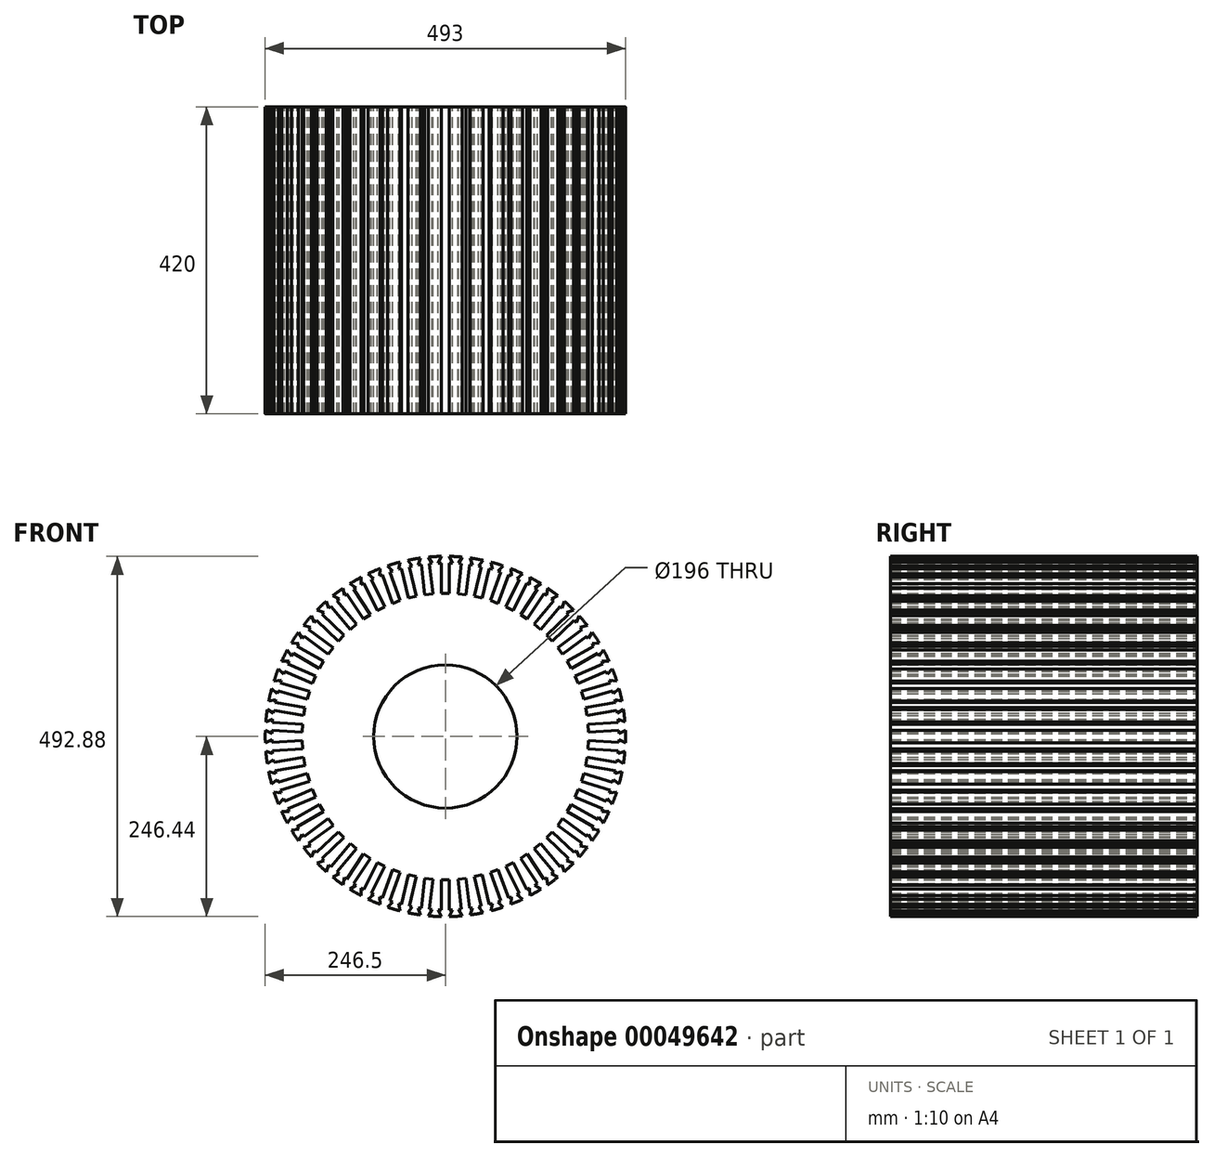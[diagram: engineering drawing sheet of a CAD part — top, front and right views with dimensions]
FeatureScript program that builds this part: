
annotation { "Feature Type Name" : "Feature", "Feature Type Description" : "" }
export const myFeature = defineFeature(function(context is Context, id is Id, definition is map)
    precondition{}
    {
        {
            var Q0;
            Q0=qCreatedBy(makeId("Front.planeOp"),FACE);
            var sketch = newSketch(context, id + "F0", { "sketchPlane" : qUnion([Q0])});
            skArc(sketch, "E0", {"start": v(-5.6, 246.44) * mm, "mid": v(-14.33, 246.08) * mm, "end": v(-23.05, 245.42) * mm});
            skLineSegment(sketch, "E1", {"start": v(0, -271.23) * mm, "end": v(0, 264.46) * mm, "construction": true});
            skLineSegment(sketch, "E2", {"start": v(0, 195.84) * mm, "end": v(-5.6, 195.84) * mm});
            skLineSegment(sketch, "E3", {"start": v(-5.6, 195.84) * mm, "end": v(-5.6, 237.27) * mm});
            skLineSegment(sketch, "E4.MirrorCS", {"start": v(5.6, 195.84) * mm, "end": v(5.6, 237.27) * mm});
            skLineSegment(sketch, "E5.MirrorCS", {"start": v(0, 195.84) * mm, "end": v(5.6, 195.84) * mm});
            skLineSegment(sketch, "E6", {"start": v(-5.6, 237.27) * mm, "end": v(-9.6, 237.27) * mm});
            skLineSegment(sketch, "E7", {"start": v(-9.6, 237.27) * mm, "end": v(-5.6, 246.44) * mm});
            skLineSegment(sketch, "E8.MirrorCS", {"start": v(9.6, 237.27) * mm, "end": v(5.6, 246.44) * mm});
            skLineSegment(sketch, "E9.MirrorCS", {"start": v(5.6, 237.27) * mm, "end": v(9.6, 237.27) * mm});
            skPoint(sketch, "E10.orphan", {"position": v(5.6, 246.44) * mm});
            skLineSegment(sketch, "E11.1.0", {"start": v(28.3, 193.86) * mm, "end": v(33.1, 235.02) * mm});
            skLineSegment(sketch, "E11.1.1", {"start": v(33.1, 235.02) * mm, "end": v(37.08, 234.55) * mm});
            skLineSegment(sketch, "E11.1.2", {"start": v(37.08, 234.55) * mm, "end": v(34.17, 244.12) * mm});
            skLineSegment(sketch, "E11.1.3", {"start": v(22.74, 194.51) * mm, "end": v(28.3, 193.86) * mm});
            skLineSegment(sketch, "E11.1.4", {"start": v(22.74, 194.51) * mm, "end": v(17.17, 195.16) * mm});
            skLineSegment(sketch, "E11.1.5", {"start": v(17.17, 195.16) * mm, "end": v(21.98, 236.32) * mm});
            skLineSegment(sketch, "E11.1.6", {"start": v(21.98, 236.32) * mm, "end": v(18.01, 236.78) * mm});
            skLineSegment(sketch, "E11.1.7", {"start": v(18.01, 236.78) * mm, "end": v(23.05, 245.42) * mm});
            skLineSegment(sketch, "E11.2.0", {"start": v(50.61, 189.27) * mm, "end": v(60.17, 229.58) * mm});
            skLineSegment(sketch, "E11.2.1", {"start": v(60.17, 229.58) * mm, "end": v(64.06, 228.66) * mm});
            skLineSegment(sketch, "E11.2.2", {"start": v(64.06, 228.66) * mm, "end": v(62.28, 238.5) * mm});
            skLineSegment(sketch, "E11.2.3", {"start": v(45.16, 190.56) * mm, "end": v(50.61, 189.27) * mm});
            skLineSegment(sketch, "E11.2.4", {"start": v(45.16, 190.56) * mm, "end": v(39.71, 191.85) * mm});
            skLineSegment(sketch, "E11.2.5", {"start": v(39.71, 191.85) * mm, "end": v(49.27, 232.17) * mm});
            skLineSegment(sketch, "E11.2.6", {"start": v(49.27, 232.17) * mm, "end": v(45.38, 233.09) * mm});
            skLineSegment(sketch, "E11.2.7", {"start": v(45.38, 233.09) * mm, "end": v(51.38, 241.09) * mm});
            skLineSegment(sketch, "E11.3.0", {"start": v(72.24, 182.11) * mm, "end": v(86.41, 221.05) * mm});
            skLineSegment(sketch, "E11.3.1", {"start": v(86.41, 221.05) * mm, "end": v(90.17, 219.68) * mm});
            skLineSegment(sketch, "E11.3.2", {"start": v(90.17, 219.68) * mm, "end": v(89.55, 229.66) * mm});
            skLineSegment(sketch, "E11.3.3", {"start": v(66.98, 184.03) * mm, "end": v(72.24, 182.11) * mm});
            skLineSegment(sketch, "E11.3.4", {"start": v(66.98, 184.03) * mm, "end": v(61.72, 185.94) * mm});
            skLineSegment(sketch, "E11.3.5", {"start": v(61.72, 185.94) * mm, "end": v(75.89, 224.88) * mm});
            skLineSegment(sketch, "E11.3.6", {"start": v(75.89, 224.88) * mm, "end": v(72.13, 226.25) * mm});
            skLineSegment(sketch, "E11.3.7", {"start": v(72.13, 226.25) * mm, "end": v(79.02, 233.49) * mm});
            skLineSegment(sketch, "E11.4.0", {"start": v(92.9, 172.5) * mm, "end": v(111.5, 209.52) * mm});
            skLineSegment(sketch, "E11.4.1", {"start": v(111.5, 209.52) * mm, "end": v(115.07, 207.72) * mm});
            skLineSegment(sketch, "E11.4.2", {"start": v(115.07, 207.72) * mm, "end": v(115.6, 217.71) * mm});
            skLineSegment(sketch, "E11.4.3", {"start": v(87.9, 175) * mm, "end": v(92.9, 172.5) * mm});
            skLineSegment(sketch, "E11.4.4", {"start": v(87.9, 175) * mm, "end": v(82.89, 177.52) * mm});
            skLineSegment(sketch, "E11.4.5", {"start": v(82.89, 177.52) * mm, "end": v(101.48, 214.55) * mm});
            skLineSegment(sketch, "E11.4.6", {"start": v(101.48, 214.55) * mm, "end": v(97.9, 216.34) * mm});
            skLineSegment(sketch, "E11.4.7", {"start": v(97.9, 216.34) * mm, "end": v(105.6, 222.74) * mm});
            skLineSegment(sketch, "E11.5.0", {"start": v(112.3, 160.54) * mm, "end": v(135.06, 195.16) * mm});
            skLineSegment(sketch, "E11.5.1", {"start": v(135.06, 195.16) * mm, "end": v(138.4, 192.96) * mm});
            skLineSegment(sketch, "E11.5.2", {"start": v(138.4, 192.96) * mm, "end": v(140.1, 202.82) * mm});
            skLineSegment(sketch, "E11.5.3", {"start": v(107.61, 163.62) * mm, "end": v(112.3, 160.54) * mm});
            skLineSegment(sketch, "E11.5.4", {"start": v(107.61, 163.62) * mm, "end": v(102.94, 166.7) * mm});
            skLineSegment(sketch, "E11.5.5", {"start": v(102.94, 166.7) * mm, "end": v(125.7, 201.31) * mm});
            skLineSegment(sketch, "E11.5.6", {"start": v(125.7, 201.31) * mm, "end": v(122.36, 203.51) * mm});
            skLineSegment(sketch, "E11.5.7", {"start": v(122.36, 203.51) * mm, "end": v(130.74, 208.97) * mm});
            skLineSegment(sketch, "E11.6.0", {"start": v(130.17, 146.42) * mm, "end": v(156.8, 178.16) * mm});
            skLineSegment(sketch, "E11.6.1", {"start": v(156.8, 178.16) * mm, "end": v(159.87, 175.59) * mm});
            skLineSegment(sketch, "E11.6.2", {"start": v(159.87, 175.59) * mm, "end": v(162.7, 185.18) * mm});
            skLineSegment(sketch, "E11.6.3", {"start": v(125.88, 150.02) * mm, "end": v(130.17, 146.42) * mm});
            skLineSegment(sketch, "E11.6.4", {"start": v(125.88, 150.02) * mm, "end": v(121.6, 153.62) * mm});
            skLineSegment(sketch, "E11.6.5", {"start": v(121.6, 153.62) * mm, "end": v(148.23, 185.36) * mm});
            skLineSegment(sketch, "E11.6.6", {"start": v(148.23, 185.36) * mm, "end": v(145.16, 187.93) * mm});
            skLineSegment(sketch, "E11.6.7", {"start": v(145.16, 187.93) * mm, "end": v(154.12, 192.38) * mm});
            skLineSegment(sketch, "E11.7.0", {"start": v(146.29, 130.32) * mm, "end": v(176.43, 158.75) * mm});
            skLineSegment(sketch, "E11.7.1", {"start": v(176.43, 158.75) * mm, "end": v(179.17, 155.84) * mm});
            skLineSegment(sketch, "E11.7.2", {"start": v(179.17, 155.84) * mm, "end": v(183.1, 165.04) * mm});
            skLineSegment(sketch, "E11.7.3", {"start": v(142.45, 134.4) * mm, "end": v(146.29, 130.32) * mm});
            skLineSegment(sketch, "E11.7.4", {"start": v(142.45, 134.4) * mm, "end": v(138.6, 138.46) * mm});
            skLineSegment(sketch, "E11.7.5", {"start": v(138.6, 138.46) * mm, "end": v(168.74, 166.9) * mm});
            skLineSegment(sketch, "E11.7.6", {"start": v(168.74, 166.9) * mm, "end": v(166, 169.8) * mm});
            skLineSegment(sketch, "E11.7.7", {"start": v(166, 169.8) * mm, "end": v(175.4, 173.19) * mm});
            skLineSegment(sketch, "E11.8.0", {"start": v(160.43, 112.45) * mm, "end": v(193.66, 137.2) * mm});
            skLineSegment(sketch, "E11.8.1", {"start": v(193.66, 137.2) * mm, "end": v(196.05, 133.99) * mm});
            skLineSegment(sketch, "E11.8.2", {"start": v(196.05, 133.99) * mm, "end": v(201.02, 142.67) * mm});
            skLineSegment(sketch, "E11.8.3", {"start": v(157.08, 116.95) * mm, "end": v(160.43, 112.45) * mm});
            skLineSegment(sketch, "E11.8.4", {"start": v(157.08, 116.95) * mm, "end": v(153.74, 121.44) * mm});
            skLineSegment(sketch, "E11.8.5", {"start": v(153.74, 121.44) * mm, "end": v(186.98, 146.18) * mm});
            skLineSegment(sketch, "E11.8.6", {"start": v(186.98, 146.18) * mm, "end": v(184.59, 149.39) * mm});
            skLineSegment(sketch, "E11.8.7", {"start": v(184.59, 149.39) * mm, "end": v(194.33, 151.65) * mm});
            skLineSegment(sketch, "E11.9.0", {"start": v(172.4, 93.07) * mm, "end": v(208.28, 113.79) * mm});
            skLineSegment(sketch, "E11.9.1", {"start": v(208.28, 113.79) * mm, "end": v(210.28, 110.32) * mm});
            skLineSegment(sketch, "E11.9.2", {"start": v(210.28, 110.32) * mm, "end": v(216.22, 118.37) * mm});
            skLineSegment(sketch, "E11.9.3", {"start": v(169.6, 97.92) * mm, "end": v(172.4, 93.07) * mm});
            skLineSegment(sketch, "E11.9.4", {"start": v(169.6, 97.92) * mm, "end": v(166.8, 102.77) * mm});
            skLineSegment(sketch, "E11.9.5", {"start": v(166.8, 102.77) * mm, "end": v(202.68, 123.49) * mm});
            skLineSegment(sketch, "E11.9.6", {"start": v(202.68, 123.49) * mm, "end": v(200.68, 126.95) * mm});
            skLineSegment(sketch, "E11.9.7", {"start": v(200.68, 126.95) * mm, "end": v(210.62, 128.07) * mm});
            skLineSegment(sketch, "E11.10.0", {"start": v(182.04, 72.42) * mm, "end": v(220.08, 88.84) * mm});
            skLineSegment(sketch, "E11.10.1", {"start": v(220.08, 88.84) * mm, "end": v(221.67, 85.16) * mm});
            skLineSegment(sketch, "E11.10.2", {"start": v(221.67, 85.16) * mm, "end": v(228.5, 92.47) * mm});
            skLineSegment(sketch, "E11.10.3", {"start": v(179.82, 77.57) * mm, "end": v(182.04, 72.42) * mm});
            skLineSegment(sketch, "E11.10.4", {"start": v(179.82, 77.57) * mm, "end": v(177.6, 82.7) * mm});
            skLineSegment(sketch, "E11.10.5", {"start": v(177.6, 82.7) * mm, "end": v(215.65, 99.12) * mm});
            skLineSegment(sketch, "E11.10.6", {"start": v(215.65, 99.12) * mm, "end": v(214.06, 102.8) * mm});
            skLineSegment(sketch, "E11.10.7", {"start": v(214.06, 102.8) * mm, "end": v(224.06, 102.75) * mm});
            skLineSegment(sketch, "E11.11.0", {"start": v(189.22, 50.8) * mm, "end": v(228.9, 62.69) * mm});
            skLineSegment(sketch, "E11.11.1", {"start": v(228.9, 62.69) * mm, "end": v(230.06, 58.85) * mm});
            skLineSegment(sketch, "E11.11.2", {"start": v(230.06, 58.85) * mm, "end": v(237.69, 65.31) * mm});
            skLineSegment(sketch, "E11.11.3", {"start": v(187.6, 56.17) * mm, "end": v(189.22, 50.8) * mm});
            skLineSegment(sketch, "E11.11.4", {"start": v(187.6, 56.17) * mm, "end": v(186, 61.53) * mm});
            skLineSegment(sketch, "E11.11.5", {"start": v(186, 61.53) * mm, "end": v(225.7, 73.41) * mm});
            skLineSegment(sketch, "E11.11.6", {"start": v(225.7, 73.41) * mm, "end": v(224.55, 77.25) * mm});
            skLineSegment(sketch, "E11.11.7", {"start": v(224.55, 77.25) * mm, "end": v(234.48, 76.04) * mm});
            skLineSegment(sketch, "E11.12.0", {"start": v(193.83, 28.5) * mm, "end": v(234.64, 35.69) * mm});
            skLineSegment(sketch, "E11.12.1", {"start": v(234.64, 35.69) * mm, "end": v(235.33, 31.75) * mm});
            skLineSegment(sketch, "E11.12.2", {"start": v(235.33, 31.75) * mm, "end": v(243.66, 37.28) * mm});
            skLineSegment(sketch, "E11.12.3", {"start": v(192.86, 34) * mm, "end": v(193.83, 28.5) * mm});
            skLineSegment(sketch, "E11.12.4", {"start": v(192.86, 34) * mm, "end": v(191.89, 39.52) * mm});
            skLineSegment(sketch, "E11.12.5", {"start": v(191.89, 39.52) * mm, "end": v(232.7, 46.72) * mm});
            skLineSegment(sketch, "E11.12.6", {"start": v(232.7, 46.72) * mm, "end": v(232, 50.66) * mm});
            skLineSegment(sketch, "E11.12.7", {"start": v(232, 50.66) * mm, "end": v(241.72, 48.3) * mm});
            skLineSegment(sketch, "E11.13.0", {"start": v(195.83, 5.8) * mm, "end": v(237.2, 8.2) * mm});
            skLineSegment(sketch, "E11.13.1", {"start": v(237.2, 8.2) * mm, "end": v(237.43, 4.21) * mm});
            skLineSegment(sketch, "E11.13.2", {"start": v(237.43, 4.21) * mm, "end": v(246.35, 8.74) * mm});
            skLineSegment(sketch, "E11.13.3", {"start": v(195.5, 11.39) * mm, "end": v(195.83, 5.8) * mm});
            skLineSegment(sketch, "E11.13.4", {"start": v(195.5, 11.39) * mm, "end": v(195.18, 16.98) * mm});
            skLineSegment(sketch, "E11.13.5", {"start": v(195.18, 16.98) * mm, "end": v(236.54, 19.39) * mm});
            skLineSegment(sketch, "E11.13.6", {"start": v(236.54, 19.39) * mm, "end": v(236.31, 23.38) * mm});
            skLineSegment(sketch, "E11.13.7", {"start": v(236.31, 23.38) * mm, "end": v(245.7, 19.92) * mm});
            skLineSegment(sketch, "E11.14.0", {"start": v(195.18, -16.98) * mm, "end": v(236.54, -19.39) * mm});
            skLineSegment(sketch, "E11.14.1", {"start": v(236.54, -19.39) * mm, "end": v(236.31, -23.38) * mm});
            skLineSegment(sketch, "E11.14.2", {"start": v(236.31, -23.38) * mm, "end": v(245.7, -19.92) * mm});
            skLineSegment(sketch, "E11.14.3", {"start": v(195.5, -11.39) * mm, "end": v(195.18, -16.98) * mm});
            skLineSegment(sketch, "E11.14.4", {"start": v(195.5, -11.39) * mm, "end": v(195.83, -5.8) * mm});
            skLineSegment(sketch, "E11.14.5", {"start": v(195.83, -5.8) * mm, "end": v(237.2, -8.2) * mm});
            skLineSegment(sketch, "E11.14.6", {"start": v(237.2, -8.2) * mm, "end": v(237.43, -4.21) * mm});
            skLineSegment(sketch, "E11.14.7", {"start": v(237.43, -4.21) * mm, "end": v(246.35, -8.74) * mm});
            skLineSegment(sketch, "E11.15.0", {"start": v(191.89, -39.52) * mm, "end": v(232.7, -46.72) * mm});
            skLineSegment(sketch, "E11.15.1", {"start": v(232.7, -46.72) * mm, "end": v(232, -50.66) * mm});
            skLineSegment(sketch, "E11.15.2", {"start": v(232, -50.66) * mm, "end": v(241.72, -48.3) * mm});
            skLineSegment(sketch, "E11.15.3", {"start": v(192.86, -34) * mm, "end": v(191.89, -39.52) * mm});
            skLineSegment(sketch, "E11.15.4", {"start": v(192.86, -34) * mm, "end": v(193.83, -28.5) * mm});
            skLineSegment(sketch, "E11.15.5", {"start": v(193.83, -28.5) * mm, "end": v(234.64, -35.69) * mm});
            skLineSegment(sketch, "E11.15.6", {"start": v(234.64, -35.69) * mm, "end": v(235.33, -31.75) * mm});
            skLineSegment(sketch, "E11.15.7", {"start": v(235.33, -31.75) * mm, "end": v(243.66, -37.28) * mm});
            skLineSegment(sketch, "E11.16.0", {"start": v(186, -61.53) * mm, "end": v(225.7, -73.41) * mm});
            skLineSegment(sketch, "E11.16.1", {"start": v(225.7, -73.41) * mm, "end": v(224.55, -77.25) * mm});
            skLineSegment(sketch, "E11.16.2", {"start": v(224.55, -77.25) * mm, "end": v(234.48, -76.04) * mm});
            skLineSegment(sketch, "E11.16.3", {"start": v(187.6, -56.17) * mm, "end": v(186, -61.53) * mm});
            skLineSegment(sketch, "E11.16.4", {"start": v(187.6, -56.17) * mm, "end": v(189.22, -50.8) * mm});
            skLineSegment(sketch, "E11.16.5", {"start": v(189.22, -50.8) * mm, "end": v(228.9, -62.69) * mm});
            skLineSegment(sketch, "E11.16.6", {"start": v(228.9, -62.69) * mm, "end": v(230.06, -58.85) * mm});
            skLineSegment(sketch, "E11.16.7", {"start": v(230.06, -58.85) * mm, "end": v(237.69, -65.31) * mm});
            skLineSegment(sketch, "E11.17.0", {"start": v(177.6, -82.7) * mm, "end": v(215.65, -99.12) * mm});
            skLineSegment(sketch, "E11.17.1", {"start": v(215.65, -99.12) * mm, "end": v(214.06, -102.8) * mm});
            skLineSegment(sketch, "E11.17.2", {"start": v(214.06, -102.8) * mm, "end": v(224.06, -102.75) * mm});
            skLineSegment(sketch, "E11.17.3", {"start": v(179.82, -77.57) * mm, "end": v(177.6, -82.7) * mm});
            skLineSegment(sketch, "E11.17.4", {"start": v(179.82, -77.57) * mm, "end": v(182.04, -72.42) * mm});
            skLineSegment(sketch, "E11.17.5", {"start": v(182.04, -72.42) * mm, "end": v(220.08, -88.84) * mm});
            skLineSegment(sketch, "E11.17.6", {"start": v(220.08, -88.84) * mm, "end": v(221.67, -85.16) * mm});
            skLineSegment(sketch, "E11.17.7", {"start": v(221.67, -85.16) * mm, "end": v(228.5, -92.47) * mm});
            skLineSegment(sketch, "E11.18.0", {"start": v(166.8, -102.77) * mm, "end": v(202.68, -123.49) * mm});
            skLineSegment(sketch, "E11.18.1", {"start": v(202.68, -123.49) * mm, "end": v(200.68, -126.95) * mm});
            skLineSegment(sketch, "E11.18.2", {"start": v(200.68, -126.95) * mm, "end": v(210.62, -128.07) * mm});
            skLineSegment(sketch, "E11.18.3", {"start": v(169.6, -97.92) * mm, "end": v(166.8, -102.77) * mm});
            skLineSegment(sketch, "E11.18.4", {"start": v(169.6, -97.92) * mm, "end": v(172.4, -93.07) * mm});
            skLineSegment(sketch, "E11.18.5", {"start": v(172.4, -93.07) * mm, "end": v(208.28, -113.79) * mm});
            skLineSegment(sketch, "E11.18.6", {"start": v(208.28, -113.79) * mm, "end": v(210.28, -110.32) * mm});
            skLineSegment(sketch, "E11.18.7", {"start": v(210.28, -110.32) * mm, "end": v(216.22, -118.37) * mm});
            skLineSegment(sketch, "E11.19.0", {"start": v(153.74, -121.44) * mm, "end": v(186.98, -146.18) * mm});
            skLineSegment(sketch, "E11.19.1", {"start": v(186.98, -146.18) * mm, "end": v(184.59, -149.39) * mm});
            skLineSegment(sketch, "E11.19.2", {"start": v(184.59, -149.39) * mm, "end": v(194.33, -151.65) * mm});
            skLineSegment(sketch, "E11.19.3", {"start": v(157.08, -116.95) * mm, "end": v(153.74, -121.44) * mm});
            skLineSegment(sketch, "E11.19.4", {"start": v(157.08, -116.95) * mm, "end": v(160.43, -112.45) * mm});
            skLineSegment(sketch, "E11.19.5", {"start": v(160.43, -112.45) * mm, "end": v(193.66, -137.2) * mm});
            skLineSegment(sketch, "E11.19.6", {"start": v(193.66, -137.2) * mm, "end": v(196.05, -133.99) * mm});
            skLineSegment(sketch, "E11.19.7", {"start": v(196.05, -133.99) * mm, "end": v(201.02, -142.67) * mm});
            skLineSegment(sketch, "E11.20.0", {"start": v(138.6, -138.46) * mm, "end": v(168.74, -166.9) * mm});
            skLineSegment(sketch, "E11.20.1", {"start": v(168.74, -166.9) * mm, "end": v(166, -169.8) * mm});
            skLineSegment(sketch, "E11.20.2", {"start": v(166, -169.8) * mm, "end": v(175.4, -173.19) * mm});
            skLineSegment(sketch, "E11.20.3", {"start": v(142.45, -134.4) * mm, "end": v(138.6, -138.46) * mm});
            skLineSegment(sketch, "E11.20.4", {"start": v(142.45, -134.4) * mm, "end": v(146.29, -130.32) * mm});
            skLineSegment(sketch, "E11.20.5", {"start": v(146.29, -130.32) * mm, "end": v(176.43, -158.75) * mm});
            skLineSegment(sketch, "E11.20.6", {"start": v(176.43, -158.75) * mm, "end": v(179.17, -155.84) * mm});
            skLineSegment(sketch, "E11.20.7", {"start": v(179.17, -155.84) * mm, "end": v(183.1, -165.04) * mm});
            skLineSegment(sketch, "E11.21.0", {"start": v(121.6, -153.62) * mm, "end": v(148.23, -185.36) * mm});
            skLineSegment(sketch, "E11.21.1", {"start": v(148.23, -185.36) * mm, "end": v(145.16, -187.93) * mm});
            skLineSegment(sketch, "E11.21.2", {"start": v(145.16, -187.93) * mm, "end": v(154.12, -192.38) * mm});
            skLineSegment(sketch, "E11.21.3", {"start": v(125.88, -150.02) * mm, "end": v(121.6, -153.62) * mm});
            skLineSegment(sketch, "E11.21.4", {"start": v(125.88, -150.02) * mm, "end": v(130.17, -146.42) * mm});
            skLineSegment(sketch, "E11.21.5", {"start": v(130.17, -146.42) * mm, "end": v(156.8, -178.16) * mm});
            skLineSegment(sketch, "E11.21.6", {"start": v(156.8, -178.16) * mm, "end": v(159.87, -175.59) * mm});
            skLineSegment(sketch, "E11.21.7", {"start": v(159.87, -175.59) * mm, "end": v(162.7, -185.18) * mm});
            skLineSegment(sketch, "E11.22.0", {"start": v(102.94, -166.7) * mm, "end": v(125.7, -201.31) * mm});
            skLineSegment(sketch, "E11.22.1", {"start": v(125.7, -201.31) * mm, "end": v(122.36, -203.51) * mm});
            skLineSegment(sketch, "E11.22.2", {"start": v(122.36, -203.51) * mm, "end": v(130.74, -208.97) * mm});
            skLineSegment(sketch, "E11.22.3", {"start": v(107.61, -163.62) * mm, "end": v(102.94, -166.7) * mm});
            skLineSegment(sketch, "E11.22.4", {"start": v(107.61, -163.62) * mm, "end": v(112.3, -160.54) * mm});
            skLineSegment(sketch, "E11.22.5", {"start": v(112.3, -160.54) * mm, "end": v(135.06, -195.16) * mm});
            skLineSegment(sketch, "E11.22.6", {"start": v(135.06, -195.16) * mm, "end": v(138.4, -192.96) * mm});
            skLineSegment(sketch, "E11.22.7", {"start": v(138.4, -192.96) * mm, "end": v(140.1, -202.82) * mm});
            skLineSegment(sketch, "E11.23.0", {"start": v(82.89, -177.52) * mm, "end": v(101.48, -214.55) * mm});
            skLineSegment(sketch, "E11.23.1", {"start": v(101.48, -214.55) * mm, "end": v(97.9, -216.34) * mm});
            skLineSegment(sketch, "E11.23.2", {"start": v(97.9, -216.34) * mm, "end": v(105.6, -222.74) * mm});
            skLineSegment(sketch, "E11.23.3", {"start": v(87.9, -175) * mm, "end": v(82.89, -177.52) * mm});
            skLineSegment(sketch, "E11.23.4", {"start": v(87.9, -175) * mm, "end": v(92.9, -172.5) * mm});
            skLineSegment(sketch, "E11.23.5", {"start": v(92.9, -172.5) * mm, "end": v(111.5, -209.52) * mm});
            skLineSegment(sketch, "E11.23.6", {"start": v(111.5, -209.52) * mm, "end": v(115.07, -207.72) * mm});
            skLineSegment(sketch, "E11.23.7", {"start": v(115.07, -207.72) * mm, "end": v(115.6, -217.71) * mm});
            skLineSegment(sketch, "E11.24.0", {"start": v(61.72, -185.94) * mm, "end": v(75.89, -224.88) * mm});
            skLineSegment(sketch, "E11.24.1", {"start": v(75.89, -224.88) * mm, "end": v(72.13, -226.25) * mm});
            skLineSegment(sketch, "E11.24.2", {"start": v(72.13, -226.25) * mm, "end": v(79.02, -233.49) * mm});
            skLineSegment(sketch, "E11.24.3", {"start": v(66.98, -184.03) * mm, "end": v(61.72, -185.94) * mm});
            skLineSegment(sketch, "E11.24.4", {"start": v(66.98, -184.03) * mm, "end": v(72.24, -182.11) * mm});
            skLineSegment(sketch, "E11.24.5", {"start": v(72.24, -182.11) * mm, "end": v(86.41, -221.05) * mm});
            skLineSegment(sketch, "E11.24.6", {"start": v(86.41, -221.05) * mm, "end": v(90.17, -219.68) * mm});
            skLineSegment(sketch, "E11.24.7", {"start": v(90.17, -219.68) * mm, "end": v(89.55, -229.66) * mm});
            skLineSegment(sketch, "E11.25.0", {"start": v(39.71, -191.85) * mm, "end": v(49.27, -232.17) * mm});
            skLineSegment(sketch, "E11.25.1", {"start": v(49.27, -232.17) * mm, "end": v(45.38, -233.09) * mm});
            skLineSegment(sketch, "E11.25.2", {"start": v(45.38, -233.09) * mm, "end": v(51.38, -241.09) * mm});
            skLineSegment(sketch, "E11.25.3", {"start": v(45.16, -190.56) * mm, "end": v(39.71, -191.85) * mm});
            skLineSegment(sketch, "E11.25.4", {"start": v(45.16, -190.56) * mm, "end": v(50.61, -189.27) * mm});
            skLineSegment(sketch, "E11.25.5", {"start": v(50.61, -189.27) * mm, "end": v(60.17, -229.58) * mm});
            skLineSegment(sketch, "E11.25.6", {"start": v(60.17, -229.58) * mm, "end": v(64.06, -228.66) * mm});
            skLineSegment(sketch, "E11.25.7", {"start": v(64.06, -228.66) * mm, "end": v(62.28, -238.5) * mm});
            skLineSegment(sketch, "E11.26.0", {"start": v(17.17, -195.16) * mm, "end": v(21.98, -236.32) * mm});
            skLineSegment(sketch, "E11.26.1", {"start": v(21.98, -236.32) * mm, "end": v(18.01, -236.78) * mm});
            skLineSegment(sketch, "E11.26.2", {"start": v(18.01, -236.78) * mm, "end": v(23.05, -245.42) * mm});
            skLineSegment(sketch, "E11.26.3", {"start": v(22.74, -194.51) * mm, "end": v(17.17, -195.16) * mm});
            skLineSegment(sketch, "E11.26.4", {"start": v(22.74, -194.51) * mm, "end": v(28.3, -193.86) * mm});
            skLineSegment(sketch, "E11.26.5", {"start": v(28.3, -193.86) * mm, "end": v(33.1, -235.02) * mm});
            skLineSegment(sketch, "E11.26.6", {"start": v(33.1, -235.02) * mm, "end": v(37.08, -234.55) * mm});
            skLineSegment(sketch, "E11.26.7", {"start": v(37.08, -234.55) * mm, "end": v(34.17, -244.12) * mm});
            skLineSegment(sketch, "E11.27.0", {"start": v(-5.6, -195.84) * mm, "end": v(-5.6, -237.27) * mm});
            skLineSegment(sketch, "E11.27.1", {"start": v(-5.6, -237.27) * mm, "end": v(-9.6, -237.27) * mm});
            skLineSegment(sketch, "E11.27.2", {"start": v(-9.6, -237.27) * mm, "end": v(-5.6, -246.44) * mm});
            skLineSegment(sketch, "E11.27.3", {"start": v(0, -195.84) * mm, "end": v(-5.6, -195.84) * mm});
            skLineSegment(sketch, "E11.27.4", {"start": v(0, -195.84) * mm, "end": v(5.6, -195.84) * mm});
            skLineSegment(sketch, "E11.27.5", {"start": v(5.6, -195.84) * mm, "end": v(5.6, -237.27) * mm});
            skLineSegment(sketch, "E11.27.6", {"start": v(5.6, -237.27) * mm, "end": v(9.6, -237.27) * mm});
            skLineSegment(sketch, "E11.27.7", {"start": v(9.6, -237.27) * mm, "end": v(5.6, -246.44) * mm});
            skLineSegment(sketch, "E11.28.0", {"start": v(-28.3, -193.86) * mm, "end": v(-33.1, -235.02) * mm});
            skLineSegment(sketch, "E11.28.1", {"start": v(-33.1, -235.02) * mm, "end": v(-37.08, -234.55) * mm});
            skLineSegment(sketch, "E11.28.2", {"start": v(-37.08, -234.55) * mm, "end": v(-34.17, -244.12) * mm});
            skLineSegment(sketch, "E11.28.3", {"start": v(-22.74, -194.51) * mm, "end": v(-28.3, -193.86) * mm});
            skLineSegment(sketch, "E11.28.4", {"start": v(-22.74, -194.51) * mm, "end": v(-17.17, -195.16) * mm});
            skLineSegment(sketch, "E11.28.5", {"start": v(-17.17, -195.16) * mm, "end": v(-21.98, -236.32) * mm});
            skLineSegment(sketch, "E11.28.6", {"start": v(-21.98, -236.32) * mm, "end": v(-18.01, -236.78) * mm});
            skLineSegment(sketch, "E11.28.7", {"start": v(-18.01, -236.78) * mm, "end": v(-23.05, -245.42) * mm});
            skLineSegment(sketch, "E11.29.0", {"start": v(-50.61, -189.27) * mm, "end": v(-60.17, -229.58) * mm});
            skLineSegment(sketch, "E11.29.1", {"start": v(-60.17, -229.58) * mm, "end": v(-64.06, -228.66) * mm});
            skLineSegment(sketch, "E11.29.2", {"start": v(-64.06, -228.66) * mm, "end": v(-62.28, -238.5) * mm});
            skLineSegment(sketch, "E11.29.3", {"start": v(-45.16, -190.56) * mm, "end": v(-50.61, -189.27) * mm});
            skLineSegment(sketch, "E11.29.4", {"start": v(-45.16, -190.56) * mm, "end": v(-39.71, -191.85) * mm});
            skLineSegment(sketch, "E11.29.5", {"start": v(-39.71, -191.85) * mm, "end": v(-49.27, -232.17) * mm});
            skLineSegment(sketch, "E11.29.6", {"start": v(-49.27, -232.17) * mm, "end": v(-45.38, -233.09) * mm});
            skLineSegment(sketch, "E11.29.7", {"start": v(-45.38, -233.09) * mm, "end": v(-51.38, -241.09) * mm});
            skLineSegment(sketch, "E11.30.0", {"start": v(-72.24, -182.11) * mm, "end": v(-86.41, -221.05) * mm});
            skLineSegment(sketch, "E11.30.1", {"start": v(-86.41, -221.05) * mm, "end": v(-90.17, -219.68) * mm});
            skLineSegment(sketch, "E11.30.2", {"start": v(-90.17, -219.68) * mm, "end": v(-89.55, -229.66) * mm});
            skLineSegment(sketch, "E11.30.3", {"start": v(-66.98, -184.03) * mm, "end": v(-72.24, -182.11) * mm});
            skLineSegment(sketch, "E11.30.4", {"start": v(-66.98, -184.03) * mm, "end": v(-61.72, -185.94) * mm});
            skLineSegment(sketch, "E11.30.5", {"start": v(-61.72, -185.94) * mm, "end": v(-75.89, -224.88) * mm});
            skLineSegment(sketch, "E11.30.6", {"start": v(-75.89, -224.88) * mm, "end": v(-72.13, -226.25) * mm});
            skLineSegment(sketch, "E11.30.7", {"start": v(-72.13, -226.25) * mm, "end": v(-79.02, -233.49) * mm});
            skLineSegment(sketch, "E11.31.0", {"start": v(-92.9, -172.5) * mm, "end": v(-111.5, -209.52) * mm});
            skLineSegment(sketch, "E11.31.1", {"start": v(-111.5, -209.52) * mm, "end": v(-115.07, -207.72) * mm});
            skLineSegment(sketch, "E11.31.2", {"start": v(-115.07, -207.72) * mm, "end": v(-115.6, -217.71) * mm});
            skLineSegment(sketch, "E11.31.3", {"start": v(-87.9, -175) * mm, "end": v(-92.9, -172.5) * mm});
            skLineSegment(sketch, "E11.31.4", {"start": v(-87.9, -175) * mm, "end": v(-82.89, -177.52) * mm});
            skLineSegment(sketch, "E11.31.5", {"start": v(-82.89, -177.52) * mm, "end": v(-101.48, -214.55) * mm});
            skLineSegment(sketch, "E11.31.6", {"start": v(-101.48, -214.55) * mm, "end": v(-97.9, -216.34) * mm});
            skLineSegment(sketch, "E11.31.7", {"start": v(-97.9, -216.34) * mm, "end": v(-105.6, -222.74) * mm});
            skLineSegment(sketch, "E11.32.0", {"start": v(-112.3, -160.54) * mm, "end": v(-135.06, -195.16) * mm});
            skLineSegment(sketch, "E11.32.1", {"start": v(-135.06, -195.16) * mm, "end": v(-138.4, -192.96) * mm});
            skLineSegment(sketch, "E11.32.2", {"start": v(-138.4, -192.96) * mm, "end": v(-140.1, -202.82) * mm});
            skLineSegment(sketch, "E11.32.3", {"start": v(-107.61, -163.62) * mm, "end": v(-112.3, -160.54) * mm});
            skLineSegment(sketch, "E11.32.4", {"start": v(-107.61, -163.62) * mm, "end": v(-102.94, -166.7) * mm});
            skLineSegment(sketch, "E11.32.5", {"start": v(-102.94, -166.7) * mm, "end": v(-125.7, -201.31) * mm});
            skLineSegment(sketch, "E11.32.6", {"start": v(-125.7, -201.31) * mm, "end": v(-122.36, -203.51) * mm});
            skLineSegment(sketch, "E11.32.7", {"start": v(-122.36, -203.51) * mm, "end": v(-130.74, -208.97) * mm});
            skLineSegment(sketch, "E11.33.0", {"start": v(-130.17, -146.42) * mm, "end": v(-156.8, -178.16) * mm});
            skLineSegment(sketch, "E11.33.1", {"start": v(-156.8, -178.16) * mm, "end": v(-159.87, -175.59) * mm});
            skLineSegment(sketch, "E11.33.2", {"start": v(-159.87, -175.59) * mm, "end": v(-162.7, -185.18) * mm});
            skLineSegment(sketch, "E11.33.3", {"start": v(-125.88, -150.02) * mm, "end": v(-130.17, -146.42) * mm});
            skLineSegment(sketch, "E11.33.4", {"start": v(-125.88, -150.02) * mm, "end": v(-121.6, -153.62) * mm});
            skLineSegment(sketch, "E11.33.5", {"start": v(-121.6, -153.62) * mm, "end": v(-148.23, -185.36) * mm});
            skLineSegment(sketch, "E11.33.6", {"start": v(-148.23, -185.36) * mm, "end": v(-145.16, -187.93) * mm});
            skLineSegment(sketch, "E11.33.7", {"start": v(-145.16, -187.93) * mm, "end": v(-154.12, -192.38) * mm});
            skLineSegment(sketch, "E11.34.0", {"start": v(-146.29, -130.32) * mm, "end": v(-176.43, -158.75) * mm});
            skLineSegment(sketch, "E11.34.1", {"start": v(-176.43, -158.75) * mm, "end": v(-179.17, -155.84) * mm});
            skLineSegment(sketch, "E11.34.2", {"start": v(-179.17, -155.84) * mm, "end": v(-183.1, -165.04) * mm});
            skLineSegment(sketch, "E11.34.3", {"start": v(-142.45, -134.4) * mm, "end": v(-146.29, -130.32) * mm});
            skLineSegment(sketch, "E11.34.4", {"start": v(-142.45, -134.4) * mm, "end": v(-138.6, -138.46) * mm});
            skLineSegment(sketch, "E11.34.5", {"start": v(-138.6, -138.46) * mm, "end": v(-168.74, -166.9) * mm});
            skLineSegment(sketch, "E11.34.6", {"start": v(-168.74, -166.9) * mm, "end": v(-166, -169.8) * mm});
            skLineSegment(sketch, "E11.34.7", {"start": v(-166, -169.8) * mm, "end": v(-175.4, -173.19) * mm});
            skLineSegment(sketch, "E11.35.0", {"start": v(-160.43, -112.45) * mm, "end": v(-193.66, -137.2) * mm});
            skLineSegment(sketch, "E11.35.1", {"start": v(-193.66, -137.2) * mm, "end": v(-196.05, -133.99) * mm});
            skLineSegment(sketch, "E11.35.2", {"start": v(-196.05, -133.99) * mm, "end": v(-201.02, -142.67) * mm});
            skLineSegment(sketch, "E11.35.3", {"start": v(-157.08, -116.95) * mm, "end": v(-160.43, -112.45) * mm});
            skLineSegment(sketch, "E11.35.4", {"start": v(-157.08, -116.95) * mm, "end": v(-153.74, -121.44) * mm});
            skLineSegment(sketch, "E11.35.5", {"start": v(-153.74, -121.44) * mm, "end": v(-186.98, -146.18) * mm});
            skLineSegment(sketch, "E11.35.6", {"start": v(-186.98, -146.18) * mm, "end": v(-184.59, -149.39) * mm});
            skLineSegment(sketch, "E11.35.7", {"start": v(-184.59, -149.39) * mm, "end": v(-194.33, -151.65) * mm});
            skLineSegment(sketch, "E11.36.0", {"start": v(-172.4, -93.07) * mm, "end": v(-208.28, -113.79) * mm});
            skLineSegment(sketch, "E11.36.1", {"start": v(-208.28, -113.79) * mm, "end": v(-210.28, -110.32) * mm});
            skLineSegment(sketch, "E11.36.2", {"start": v(-210.28, -110.32) * mm, "end": v(-216.22, -118.37) * mm});
            skLineSegment(sketch, "E11.36.3", {"start": v(-169.6, -97.92) * mm, "end": v(-172.4, -93.07) * mm});
            skLineSegment(sketch, "E11.36.4", {"start": v(-169.6, -97.92) * mm, "end": v(-166.8, -102.77) * mm});
            skLineSegment(sketch, "E11.36.5", {"start": v(-166.8, -102.77) * mm, "end": v(-202.68, -123.49) * mm});
            skLineSegment(sketch, "E11.36.6", {"start": v(-202.68, -123.49) * mm, "end": v(-200.68, -126.95) * mm});
            skLineSegment(sketch, "E11.36.7", {"start": v(-200.68, -126.95) * mm, "end": v(-210.62, -128.07) * mm});
            skLineSegment(sketch, "E11.37.0", {"start": v(-182.04, -72.42) * mm, "end": v(-220.08, -88.84) * mm});
            skLineSegment(sketch, "E11.37.1", {"start": v(-220.08, -88.84) * mm, "end": v(-221.67, -85.16) * mm});
            skLineSegment(sketch, "E11.37.2", {"start": v(-221.67, -85.16) * mm, "end": v(-228.5, -92.47) * mm});
            skLineSegment(sketch, "E11.37.3", {"start": v(-179.82, -77.57) * mm, "end": v(-182.04, -72.42) * mm});
            skLineSegment(sketch, "E11.37.4", {"start": v(-179.82, -77.57) * mm, "end": v(-177.6, -82.7) * mm});
            skLineSegment(sketch, "E11.37.5", {"start": v(-177.6, -82.7) * mm, "end": v(-215.65, -99.12) * mm});
            skLineSegment(sketch, "E11.37.6", {"start": v(-215.65, -99.12) * mm, "end": v(-214.06, -102.8) * mm});
            skLineSegment(sketch, "E11.37.7", {"start": v(-214.06, -102.8) * mm, "end": v(-224.06, -102.75) * mm});
            skLineSegment(sketch, "E11.38.0", {"start": v(-189.22, -50.8) * mm, "end": v(-228.9, -62.69) * mm});
            skLineSegment(sketch, "E11.38.1", {"start": v(-228.9, -62.69) * mm, "end": v(-230.06, -58.85) * mm});
            skLineSegment(sketch, "E11.38.2", {"start": v(-230.06, -58.85) * mm, "end": v(-237.69, -65.31) * mm});
            skLineSegment(sketch, "E11.38.3", {"start": v(-187.6, -56.17) * mm, "end": v(-189.22, -50.8) * mm});
            skLineSegment(sketch, "E11.38.4", {"start": v(-187.6, -56.17) * mm, "end": v(-186, -61.53) * mm});
            skLineSegment(sketch, "E11.38.5", {"start": v(-186, -61.53) * mm, "end": v(-225.7, -73.41) * mm});
            skLineSegment(sketch, "E11.38.6", {"start": v(-225.7, -73.41) * mm, "end": v(-224.55, -77.25) * mm});
            skLineSegment(sketch, "E11.38.7", {"start": v(-224.55, -77.25) * mm, "end": v(-234.48, -76.04) * mm});
            skLineSegment(sketch, "E11.39.0", {"start": v(-193.83, -28.5) * mm, "end": v(-234.64, -35.69) * mm});
            skLineSegment(sketch, "E11.39.1", {"start": v(-234.64, -35.69) * mm, "end": v(-235.33, -31.75) * mm});
            skLineSegment(sketch, "E11.39.2", {"start": v(-235.33, -31.75) * mm, "end": v(-243.66, -37.28) * mm});
            skLineSegment(sketch, "E11.39.3", {"start": v(-192.86, -34) * mm, "end": v(-193.83, -28.5) * mm});
            skLineSegment(sketch, "E11.39.4", {"start": v(-192.86, -34) * mm, "end": v(-191.89, -39.52) * mm});
            skLineSegment(sketch, "E11.39.5", {"start": v(-191.89, -39.52) * mm, "end": v(-232.7, -46.72) * mm});
            skLineSegment(sketch, "E11.39.6", {"start": v(-232.7, -46.72) * mm, "end": v(-232, -50.66) * mm});
            skLineSegment(sketch, "E11.39.7", {"start": v(-232, -50.66) * mm, "end": v(-241.72, -48.3) * mm});
            skLineSegment(sketch, "E11.40.0", {"start": v(-195.83, -5.8) * mm, "end": v(-237.2, -8.2) * mm});
            skLineSegment(sketch, "E11.40.1", {"start": v(-237.2, -8.2) * mm, "end": v(-237.43, -4.21) * mm});
            skLineSegment(sketch, "E11.40.2", {"start": v(-237.43, -4.21) * mm, "end": v(-246.35, -8.74) * mm});
            skLineSegment(sketch, "E11.40.3", {"start": v(-195.5, -11.39) * mm, "end": v(-195.83, -5.8) * mm});
            skLineSegment(sketch, "E11.40.4", {"start": v(-195.5, -11.39) * mm, "end": v(-195.18, -16.98) * mm});
            skLineSegment(sketch, "E11.40.5", {"start": v(-195.18, -16.98) * mm, "end": v(-236.54, -19.39) * mm});
            skLineSegment(sketch, "E11.40.6", {"start": v(-236.54, -19.39) * mm, "end": v(-236.31, -23.38) * mm});
            skLineSegment(sketch, "E11.40.7", {"start": v(-236.31, -23.38) * mm, "end": v(-245.7, -19.92) * mm});
            skLineSegment(sketch, "E11.41.0", {"start": v(-195.18, 16.98) * mm, "end": v(-236.54, 19.39) * mm});
            skLineSegment(sketch, "E11.41.1", {"start": v(-236.54, 19.39) * mm, "end": v(-236.31, 23.38) * mm});
            skLineSegment(sketch, "E11.41.2", {"start": v(-236.31, 23.38) * mm, "end": v(-245.7, 19.92) * mm});
            skLineSegment(sketch, "E11.41.3", {"start": v(-195.5, 11.39) * mm, "end": v(-195.18, 16.98) * mm});
            skLineSegment(sketch, "E11.41.4", {"start": v(-195.5, 11.39) * mm, "end": v(-195.83, 5.8) * mm});
            skLineSegment(sketch, "E11.41.5", {"start": v(-195.83, 5.8) * mm, "end": v(-237.2, 8.2) * mm});
            skLineSegment(sketch, "E11.41.6", {"start": v(-237.2, 8.2) * mm, "end": v(-237.43, 4.21) * mm});
            skLineSegment(sketch, "E11.41.7", {"start": v(-237.43, 4.21) * mm, "end": v(-246.35, 8.74) * mm});
            skLineSegment(sketch, "E11.42.0", {"start": v(-191.89, 39.52) * mm, "end": v(-232.7, 46.72) * mm});
            skLineSegment(sketch, "E11.42.1", {"start": v(-232.7, 46.72) * mm, "end": v(-232, 50.66) * mm});
            skLineSegment(sketch, "E11.42.2", {"start": v(-232, 50.66) * mm, "end": v(-241.72, 48.3) * mm});
            skLineSegment(sketch, "E11.42.3", {"start": v(-192.86, 34) * mm, "end": v(-191.89, 39.52) * mm});
            skLineSegment(sketch, "E11.42.4", {"start": v(-192.86, 34) * mm, "end": v(-193.83, 28.5) * mm});
            skLineSegment(sketch, "E11.42.5", {"start": v(-193.83, 28.5) * mm, "end": v(-234.64, 35.69) * mm});
            skLineSegment(sketch, "E11.42.6", {"start": v(-234.64, 35.69) * mm, "end": v(-235.33, 31.75) * mm});
            skLineSegment(sketch, "E11.42.7", {"start": v(-235.33, 31.75) * mm, "end": v(-243.66, 37.28) * mm});
            skLineSegment(sketch, "E11.43.0", {"start": v(-186, 61.53) * mm, "end": v(-225.7, 73.41) * mm});
            skLineSegment(sketch, "E11.43.1", {"start": v(-225.7, 73.41) * mm, "end": v(-224.55, 77.25) * mm});
            skLineSegment(sketch, "E11.43.2", {"start": v(-224.55, 77.25) * mm, "end": v(-234.48, 76.04) * mm});
            skLineSegment(sketch, "E11.43.3", {"start": v(-187.6, 56.17) * mm, "end": v(-186, 61.53) * mm});
            skLineSegment(sketch, "E11.43.4", {"start": v(-187.6, 56.17) * mm, "end": v(-189.22, 50.8) * mm});
            skLineSegment(sketch, "E11.43.5", {"start": v(-189.22, 50.8) * mm, "end": v(-228.9, 62.69) * mm});
            skLineSegment(sketch, "E11.43.6", {"start": v(-228.9, 62.69) * mm, "end": v(-230.06, 58.85) * mm});
            skLineSegment(sketch, "E11.43.7", {"start": v(-230.06, 58.85) * mm, "end": v(-237.69, 65.31) * mm});
            skLineSegment(sketch, "E11.44.0", {"start": v(-177.6, 82.7) * mm, "end": v(-215.65, 99.12) * mm});
            skLineSegment(sketch, "E11.44.1", {"start": v(-215.65, 99.12) * mm, "end": v(-214.06, 102.8) * mm});
            skLineSegment(sketch, "E11.44.2", {"start": v(-214.06, 102.8) * mm, "end": v(-224.06, 102.75) * mm});
            skLineSegment(sketch, "E11.44.3", {"start": v(-179.82, 77.57) * mm, "end": v(-177.6, 82.7) * mm});
            skLineSegment(sketch, "E11.44.4", {"start": v(-179.82, 77.57) * mm, "end": v(-182.04, 72.42) * mm});
            skLineSegment(sketch, "E11.44.5", {"start": v(-182.04, 72.42) * mm, "end": v(-220.08, 88.84) * mm});
            skLineSegment(sketch, "E11.44.6", {"start": v(-220.08, 88.84) * mm, "end": v(-221.67, 85.16) * mm});
            skLineSegment(sketch, "E11.44.7", {"start": v(-221.67, 85.16) * mm, "end": v(-228.5, 92.47) * mm});
            skLineSegment(sketch, "E11.45.0", {"start": v(-166.8, 102.77) * mm, "end": v(-202.68, 123.49) * mm});
            skLineSegment(sketch, "E11.45.1", {"start": v(-202.68, 123.49) * mm, "end": v(-200.68, 126.95) * mm});
            skLineSegment(sketch, "E11.45.2", {"start": v(-200.68, 126.95) * mm, "end": v(-210.62, 128.07) * mm});
            skLineSegment(sketch, "E11.45.3", {"start": v(-169.6, 97.92) * mm, "end": v(-166.8, 102.77) * mm});
            skLineSegment(sketch, "E11.45.4", {"start": v(-169.6, 97.92) * mm, "end": v(-172.4, 93.07) * mm});
            skLineSegment(sketch, "E11.45.5", {"start": v(-172.4, 93.07) * mm, "end": v(-208.28, 113.79) * mm});
            skLineSegment(sketch, "E11.45.6", {"start": v(-208.28, 113.79) * mm, "end": v(-210.28, 110.32) * mm});
            skLineSegment(sketch, "E11.45.7", {"start": v(-210.28, 110.32) * mm, "end": v(-216.22, 118.37) * mm});
            skLineSegment(sketch, "E11.46.0", {"start": v(-153.74, 121.44) * mm, "end": v(-186.98, 146.18) * mm});
            skLineSegment(sketch, "E11.46.1", {"start": v(-186.98, 146.18) * mm, "end": v(-184.59, 149.39) * mm});
            skLineSegment(sketch, "E11.46.2", {"start": v(-184.59, 149.39) * mm, "end": v(-194.33, 151.65) * mm});
            skLineSegment(sketch, "E11.46.3", {"start": v(-157.08, 116.95) * mm, "end": v(-153.74, 121.44) * mm});
            skLineSegment(sketch, "E11.46.4", {"start": v(-157.08, 116.95) * mm, "end": v(-160.43, 112.45) * mm});
            skLineSegment(sketch, "E11.46.5", {"start": v(-160.43, 112.45) * mm, "end": v(-193.66, 137.2) * mm});
            skLineSegment(sketch, "E11.46.6", {"start": v(-193.66, 137.2) * mm, "end": v(-196.05, 133.99) * mm});
            skLineSegment(sketch, "E11.46.7", {"start": v(-196.05, 133.99) * mm, "end": v(-201.02, 142.67) * mm});
            skLineSegment(sketch, "E11.47.0", {"start": v(-138.6, 138.46) * mm, "end": v(-168.74, 166.9) * mm});
            skLineSegment(sketch, "E11.47.1", {"start": v(-168.74, 166.9) * mm, "end": v(-166, 169.8) * mm});
            skLineSegment(sketch, "E11.47.2", {"start": v(-166, 169.8) * mm, "end": v(-175.4, 173.19) * mm});
            skLineSegment(sketch, "E11.47.3", {"start": v(-142.45, 134.4) * mm, "end": v(-138.6, 138.46) * mm});
            skLineSegment(sketch, "E11.47.4", {"start": v(-142.45, 134.4) * mm, "end": v(-146.29, 130.32) * mm});
            skLineSegment(sketch, "E11.47.5", {"start": v(-146.29, 130.32) * mm, "end": v(-176.43, 158.75) * mm});
            skLineSegment(sketch, "E11.47.6", {"start": v(-176.43, 158.75) * mm, "end": v(-179.17, 155.84) * mm});
            skLineSegment(sketch, "E11.47.7", {"start": v(-179.17, 155.84) * mm, "end": v(-183.1, 165.04) * mm});
            skLineSegment(sketch, "E11.48.0", {"start": v(-121.6, 153.62) * mm, "end": v(-148.23, 185.36) * mm});
            skLineSegment(sketch, "E11.48.1", {"start": v(-148.23, 185.36) * mm, "end": v(-145.16, 187.93) * mm});
            skLineSegment(sketch, "E11.48.2", {"start": v(-145.16, 187.93) * mm, "end": v(-154.12, 192.38) * mm});
            skLineSegment(sketch, "E11.48.3", {"start": v(-125.88, 150.02) * mm, "end": v(-121.6, 153.62) * mm});
            skLineSegment(sketch, "E11.48.4", {"start": v(-125.88, 150.02) * mm, "end": v(-130.17, 146.42) * mm});
            skLineSegment(sketch, "E11.48.5", {"start": v(-130.17, 146.42) * mm, "end": v(-156.8, 178.16) * mm});
            skLineSegment(sketch, "E11.48.6", {"start": v(-156.8, 178.16) * mm, "end": v(-159.87, 175.59) * mm});
            skLineSegment(sketch, "E11.48.7", {"start": v(-159.87, 175.59) * mm, "end": v(-162.7, 185.18) * mm});
            skLineSegment(sketch, "E11.49.0", {"start": v(-102.94, 166.7) * mm, "end": v(-125.7, 201.31) * mm});
            skLineSegment(sketch, "E11.49.1", {"start": v(-125.7, 201.31) * mm, "end": v(-122.36, 203.51) * mm});
            skLineSegment(sketch, "E11.49.2", {"start": v(-122.36, 203.51) * mm, "end": v(-130.74, 208.97) * mm});
            skLineSegment(sketch, "E11.49.3", {"start": v(-107.61, 163.62) * mm, "end": v(-102.94, 166.7) * mm});
            skLineSegment(sketch, "E11.49.4", {"start": v(-107.61, 163.62) * mm, "end": v(-112.3, 160.54) * mm});
            skLineSegment(sketch, "E11.49.5", {"start": v(-112.3, 160.54) * mm, "end": v(-135.06, 195.16) * mm});
            skLineSegment(sketch, "E11.49.6", {"start": v(-135.06, 195.16) * mm, "end": v(-138.4, 192.96) * mm});
            skLineSegment(sketch, "E11.49.7", {"start": v(-138.4, 192.96) * mm, "end": v(-140.1, 202.82) * mm});
            skLineSegment(sketch, "E11.50.0", {"start": v(-82.89, 177.52) * mm, "end": v(-101.48, 214.55) * mm});
            skLineSegment(sketch, "E11.50.1", {"start": v(-101.48, 214.55) * mm, "end": v(-97.9, 216.34) * mm});
            skLineSegment(sketch, "E11.50.2", {"start": v(-97.9, 216.34) * mm, "end": v(-105.6, 222.74) * mm});
            skLineSegment(sketch, "E11.50.3", {"start": v(-87.9, 175) * mm, "end": v(-82.89, 177.52) * mm});
            skLineSegment(sketch, "E11.50.4", {"start": v(-87.9, 175) * mm, "end": v(-92.9, 172.5) * mm});
            skLineSegment(sketch, "E11.50.5", {"start": v(-92.9, 172.5) * mm, "end": v(-111.5, 209.52) * mm});
            skLineSegment(sketch, "E11.50.6", {"start": v(-111.5, 209.52) * mm, "end": v(-115.07, 207.72) * mm});
            skLineSegment(sketch, "E11.50.7", {"start": v(-115.07, 207.72) * mm, "end": v(-115.6, 217.71) * mm});
            skLineSegment(sketch, "E11.51.0", {"start": v(-61.72, 185.94) * mm, "end": v(-75.89, 224.88) * mm});
            skLineSegment(sketch, "E11.51.1", {"start": v(-75.89, 224.88) * mm, "end": v(-72.13, 226.25) * mm});
            skLineSegment(sketch, "E11.51.2", {"start": v(-72.13, 226.25) * mm, "end": v(-79.02, 233.49) * mm});
            skLineSegment(sketch, "E11.51.3", {"start": v(-66.98, 184.03) * mm, "end": v(-61.72, 185.94) * mm});
            skLineSegment(sketch, "E11.51.4", {"start": v(-66.98, 184.03) * mm, "end": v(-72.24, 182.11) * mm});
            skLineSegment(sketch, "E11.51.5", {"start": v(-72.24, 182.11) * mm, "end": v(-86.41, 221.05) * mm});
            skLineSegment(sketch, "E11.51.6", {"start": v(-86.41, 221.05) * mm, "end": v(-90.17, 219.68) * mm});
            skLineSegment(sketch, "E11.51.7", {"start": v(-90.17, 219.68) * mm, "end": v(-89.55, 229.66) * mm});
            skLineSegment(sketch, "E11.52.0", {"start": v(-39.71, 191.85) * mm, "end": v(-49.27, 232.17) * mm});
            skLineSegment(sketch, "E11.52.1", {"start": v(-49.27, 232.17) * mm, "end": v(-45.38, 233.09) * mm});
            skLineSegment(sketch, "E11.52.2", {"start": v(-45.38, 233.09) * mm, "end": v(-51.38, 241.09) * mm});
            skLineSegment(sketch, "E11.52.3", {"start": v(-45.16, 190.56) * mm, "end": v(-39.71, 191.85) * mm});
            skLineSegment(sketch, "E11.52.4", {"start": v(-45.16, 190.56) * mm, "end": v(-50.61, 189.27) * mm});
            skLineSegment(sketch, "E11.52.5", {"start": v(-50.61, 189.27) * mm, "end": v(-60.17, 229.58) * mm});
            skLineSegment(sketch, "E11.52.6", {"start": v(-60.17, 229.58) * mm, "end": v(-64.06, 228.66) * mm});
            skLineSegment(sketch, "E11.52.7", {"start": v(-64.06, 228.66) * mm, "end": v(-62.28, 238.5) * mm});
            skLineSegment(sketch, "E11.53.0", {"start": v(-17.17, 195.16) * mm, "end": v(-21.98, 236.32) * mm});
            skLineSegment(sketch, "E11.53.1", {"start": v(-21.98, 236.32) * mm, "end": v(-18.01, 236.78) * mm});
            skLineSegment(sketch, "E11.53.2", {"start": v(-18.01, 236.78) * mm, "end": v(-23.05, 245.42) * mm});
            skLineSegment(sketch, "E11.53.3", {"start": v(-22.74, 194.51) * mm, "end": v(-17.17, 195.16) * mm});
            skLineSegment(sketch, "E11.53.4", {"start": v(-22.74, 194.51) * mm, "end": v(-28.3, 193.86) * mm});
            skLineSegment(sketch, "E11.53.5", {"start": v(-28.3, 193.86) * mm, "end": v(-33.1, 235.02) * mm});
            skLineSegment(sketch, "E11.53.6", {"start": v(-33.1, 235.02) * mm, "end": v(-37.08, 234.55) * mm});
            skLineSegment(sketch, "E11.53.7", {"start": v(-37.08, 234.55) * mm, "end": v(-34.17, 244.12) * mm});
            skLineSegment(sketch, "E11.anchor1", {"start": v(0, 0) * mm, "end": v(5.6, 195.84) * mm, "construction": true});
            skLineSegment(sketch, "E11.anchor2", {"start": v(0, 0) * mm, "end": v(-17.17, 195.16) * mm, "construction": true});
            skArc(sketch, "E12.trimOffspring", {"start": v(-34.17, 244.12) * mm, "mid": v(-42.8, 242.76) * mm, "end": v(-51.38, 241.09) * mm});
            skArc(sketch, "E13.trimOffspring", {"start": v(-62.28, 238.5) * mm, "mid": v(-70.7, 236.14) * mm, "end": v(-79.02, 233.49) * mm});
            skArc(sketch, "E14.trimOffspring", {"start": v(-89.55, 229.66) * mm, "mid": v(-97.63, 226.34) * mm, "end": v(-105.6, 222.74) * mm});
            skArc(sketch, "E15.trimOffspring", {"start": v(-115.6, 217.71) * mm, "mid": v(-123.25, 213.48) * mm, "end": v(-130.74, 208.97) * mm});
            skArc(sketch, "E16.trimOffspring", {"start": v(-140.1, 202.82) * mm, "mid": v(-147.2, 197.72) * mm, "end": v(-154.12, 192.38) * mm});
            skArc(sketch, "E17.trimOffspring", {"start": v(-162.7, 185.18) * mm, "mid": v(-169.16, 179.3) * mm, "end": v(-175.4, 173.19) * mm});
            skArc(sketch, "E18.trimOffspring", {"start": v(-183.1, 165.04) * mm, "mid": v(-188.83, 158.45) * mm, "end": v(-194.33, 151.65) * mm});
            skArc(sketch, "E19.trimOffspring", {"start": v(-201.02, 142.67) * mm, "mid": v(-205.95, 135.45) * mm, "end": v(-210.62, 128.07) * mm});
            skArc(sketch, "E20.trimOffspring", {"start": v(-216.22, 118.37) * mm, "mid": v(-220.28, 110.63) * mm, "end": v(-224.06, 102.75) * mm});
            skArc(sketch, "E21.trimOffspring", {"start": v(-228.5, 92.47) * mm, "mid": v(-231.63, 84.3) * mm, "end": v(-234.48, 76.04) * mm});
            skArc(sketch, "E22.trimOffspring", {"start": v(-237.69, 65.31) * mm, "mid": v(-239.86, 56.85) * mm, "end": v(-241.72, 48.3) * mm});
            skArc(sketch, "E23.trimOffspring", {"start": v(-243.66, 37.28) * mm, "mid": v(-244.83, 28.62) * mm, "end": v(-245.7, 19.92) * mm});
            skArc(sketch, "E24.trimOffspring", {"start": v(-246.35, 8.74) * mm, "mid": v(-246.5, 0) * mm, "end": v(-246.35, -8.74) * mm});
            skArc(sketch, "E25.trimOffspring", {"start": v(-245.7, -19.92) * mm, "mid": v(-244.83, -28.62) * mm, "end": v(-243.66, -37.28) * mm});
            skArc(sketch, "E26.trimOffspring", {"start": v(-241.72, -48.3) * mm, "mid": v(-239.86, -56.85) * mm, "end": v(-237.69, -65.31) * mm});
            skArc(sketch, "E27.trimOffspring", {"start": v(-234.48, -76.04) * mm, "mid": v(-231.63, -84.3) * mm, "end": v(-228.5, -92.47) * mm});
            skArc(sketch, "E28.trimOffspring", {"start": v(-224.06, -102.75) * mm, "mid": v(-220.28, -110.63) * mm, "end": v(-216.22, -118.37) * mm});
            skArc(sketch, "E29.trimOffspring", {"start": v(-210.62, -128.07) * mm, "mid": v(-205.95, -135.45) * mm, "end": v(-201.02, -142.67) * mm});
            skArc(sketch, "E30.trimOffspring", {"start": v(-194.33, -151.65) * mm, "mid": v(-188.83, -158.45) * mm, "end": v(-183.1, -165.04) * mm});
            skArc(sketch, "E31.trimOffspring", {"start": v(-175.4, -173.19) * mm, "mid": v(-169.16, -179.3) * mm, "end": v(-162.7, -185.18) * mm});
            skArc(sketch, "E32.trimOffspring", {"start": v(-154.12, -192.38) * mm, "mid": v(-147.2, -197.72) * mm, "end": v(-140.1, -202.82) * mm});
            skArc(sketch, "E33.trimOffspring", {"start": v(-130.74, -208.97) * mm, "mid": v(-123.25, -213.48) * mm, "end": v(-115.6, -217.71) * mm});
            skArc(sketch, "E34.trimOffspring", {"start": v(-105.6, -222.74) * mm, "mid": v(-97.63, -226.34) * mm, "end": v(-89.55, -229.66) * mm});
            skArc(sketch, "E35.trimOffspring", {"start": v(-79.02, -233.49) * mm, "mid": v(-70.7, -236.14) * mm, "end": v(-62.28, -238.5) * mm});
            skArc(sketch, "E36.trimOffspring", {"start": v(-51.38, -241.09) * mm, "mid": v(-42.8, -242.76) * mm, "end": v(-34.17, -244.12) * mm});
            skArc(sketch, "E37.trimOffspring", {"start": v(-23.05, -245.42) * mm, "mid": v(-14.33, -246.08) * mm, "end": v(-5.6, -246.44) * mm});
            skArc(sketch, "E38.trimOffspring", {"start": v(5.6, -246.44) * mm, "mid": v(14.33, -246.08) * mm, "end": v(23.05, -245.42) * mm});
            skArc(sketch, "E39.trimOffspring", {"start": v(34.17, -244.12) * mm, "mid": v(42.8, -242.76) * mm, "end": v(51.38, -241.09) * mm});
            skArc(sketch, "E40.trimOffspring", {"start": v(62.28, -238.5) * mm, "mid": v(70.7, -236.14) * mm, "end": v(79.02, -233.49) * mm});
            skArc(sketch, "E41.trimOffspring", {"start": v(89.55, -229.66) * mm, "mid": v(97.63, -226.34) * mm, "end": v(105.6, -222.74) * mm});
            skArc(sketch, "E42.trimOffspring", {"start": v(115.6, -217.71) * mm, "mid": v(123.25, -213.48) * mm, "end": v(130.74, -208.97) * mm});
            skArc(sketch, "E43.trimOffspring", {"start": v(140.1, -202.82) * mm, "mid": v(147.2, -197.72) * mm, "end": v(154.12, -192.38) * mm});
            skArc(sketch, "E44.trimOffspring", {"start": v(162.7, -185.18) * mm, "mid": v(169.16, -179.3) * mm, "end": v(175.4, -173.19) * mm});
            skArc(sketch, "E45.trimOffspring", {"start": v(183.1, -165.04) * mm, "mid": v(188.83, -158.45) * mm, "end": v(194.33, -151.65) * mm});
            skArc(sketch, "E46.trimOffspring", {"start": v(201.02, -142.67) * mm, "mid": v(205.95, -135.45) * mm, "end": v(210.62, -128.07) * mm});
            skArc(sketch, "E47.trimOffspring", {"start": v(216.22, -118.37) * mm, "mid": v(220.28, -110.63) * mm, "end": v(224.06, -102.75) * mm});
            skArc(sketch, "E48.trimOffspring", {"start": v(228.5, -92.47) * mm, "mid": v(231.63, -84.3) * mm, "end": v(234.48, -76.04) * mm});
            skArc(sketch, "E49.trimOffspring", {"start": v(237.69, -65.31) * mm, "mid": v(239.86, -56.85) * mm, "end": v(241.72, -48.3) * mm});
            skArc(sketch, "E50.trimOffspring", {"start": v(243.66, -37.28) * mm, "mid": v(244.83, -28.62) * mm, "end": v(245.7, -19.92) * mm});
            skArc(sketch, "E51.trimOffspring", {"start": v(246.35, -8.74) * mm, "mid": v(246.5, 0) * mm, "end": v(246.35, 8.74) * mm});
            skArc(sketch, "E52.trimOffspring", {"start": v(245.7, 19.92) * mm, "mid": v(244.83, 28.62) * mm, "end": v(243.66, 37.28) * mm});
            skArc(sketch, "E53.trimOffspring", {"start": v(241.72, 48.3) * mm, "mid": v(239.86, 56.85) * mm, "end": v(237.69, 65.31) * mm});
            skArc(sketch, "E54.trimOffspring", {"start": v(234.48, 76.04) * mm, "mid": v(231.63, 84.3) * mm, "end": v(228.5, 92.47) * mm});
            skArc(sketch, "E55.trimOffspring", {"start": v(224.06, 102.75) * mm, "mid": v(220.28, 110.63) * mm, "end": v(216.22, 118.37) * mm});
            skArc(sketch, "E56.trimOffspring", {"start": v(210.62, 128.07) * mm, "mid": v(205.95, 135.45) * mm, "end": v(201.02, 142.67) * mm});
            skArc(sketch, "E57.trimOffspring", {"start": v(194.33, 151.65) * mm, "mid": v(188.83, 158.45) * mm, "end": v(183.1, 165.04) * mm});
            skArc(sketch, "E58.trimOffspring", {"start": v(175.4, 173.19) * mm, "mid": v(169.16, 179.3) * mm, "end": v(162.7, 185.18) * mm});
            skArc(sketch, "E59.trimOffspring", {"start": v(154.12, 192.38) * mm, "mid": v(147.2, 197.72) * mm, "end": v(140.1, 202.82) * mm});
            skArc(sketch, "E60.trimOffspring", {"start": v(130.74, 208.97) * mm, "mid": v(123.25, 213.48) * mm, "end": v(115.6, 217.71) * mm});
            skArc(sketch, "E61.trimOffspring", {"start": v(105.6, 222.74) * mm, "mid": v(97.63, 226.34) * mm, "end": v(89.55, 229.66) * mm});
            skArc(sketch, "E62.trimOffspring", {"start": v(79.02, 233.49) * mm, "mid": v(70.7, 236.14) * mm, "end": v(62.28, 238.5) * mm});
            skArc(sketch, "E63.trimOffspring", {"start": v(51.38, 241.09) * mm, "mid": v(42.8, 242.76) * mm, "end": v(34.17, 244.12) * mm});
            skArc(sketch, "E64.trimOffspring", {"start": v(23.05, 245.42) * mm, "mid": v(14.33, 246.08) * mm, "end": v(5.6, 246.44) * mm});
            skCircle(sketch, "E65", {"center": v(0, 0) * mm, "radius": 98 * mm});
            skSolve(sketch);
        }
        {
            var Q0;
            Q0 = qSketchRegion(id + "F0", true);
            extrude(context, id + "F1", {"entities" : qUnion([Q0]), "depth" : 420 * mm});
        }
    });
